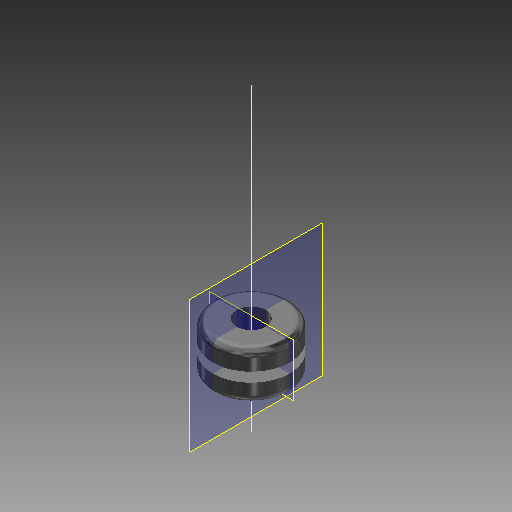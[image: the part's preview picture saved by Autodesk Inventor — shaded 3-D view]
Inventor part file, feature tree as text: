
AUTODESK INVENTOR PART (.ipt)
format: ipt  version: 2017 (Build 210142000, 142)  size: 144,384 bytes
history: native  units: in
note: dims shown in document units (in); Inventor stores cm internally (conversion verified against a paired STEP export)
features: plane x2, revolve x1, sketch x1, other x1
ambient origin geometry x8: Origin, YZ Plane, XZ Plane, XY Plane, X Axis, Y Axis, Z Axis, Center Point
bodies: Solid1 (feature_tree)
feature tree (5):
  plane  "Work Plane2"
  revolve  "Revolution1"  Angle=90.0deg
  plane  "Work Plane3"
  sketch  "Sketch2"  dims[d0=0.05in d1=90.0deg d2=0.05in d4=0.1562in d5=0.3125in d6=90.0deg]
  other  "Work Axis2"
